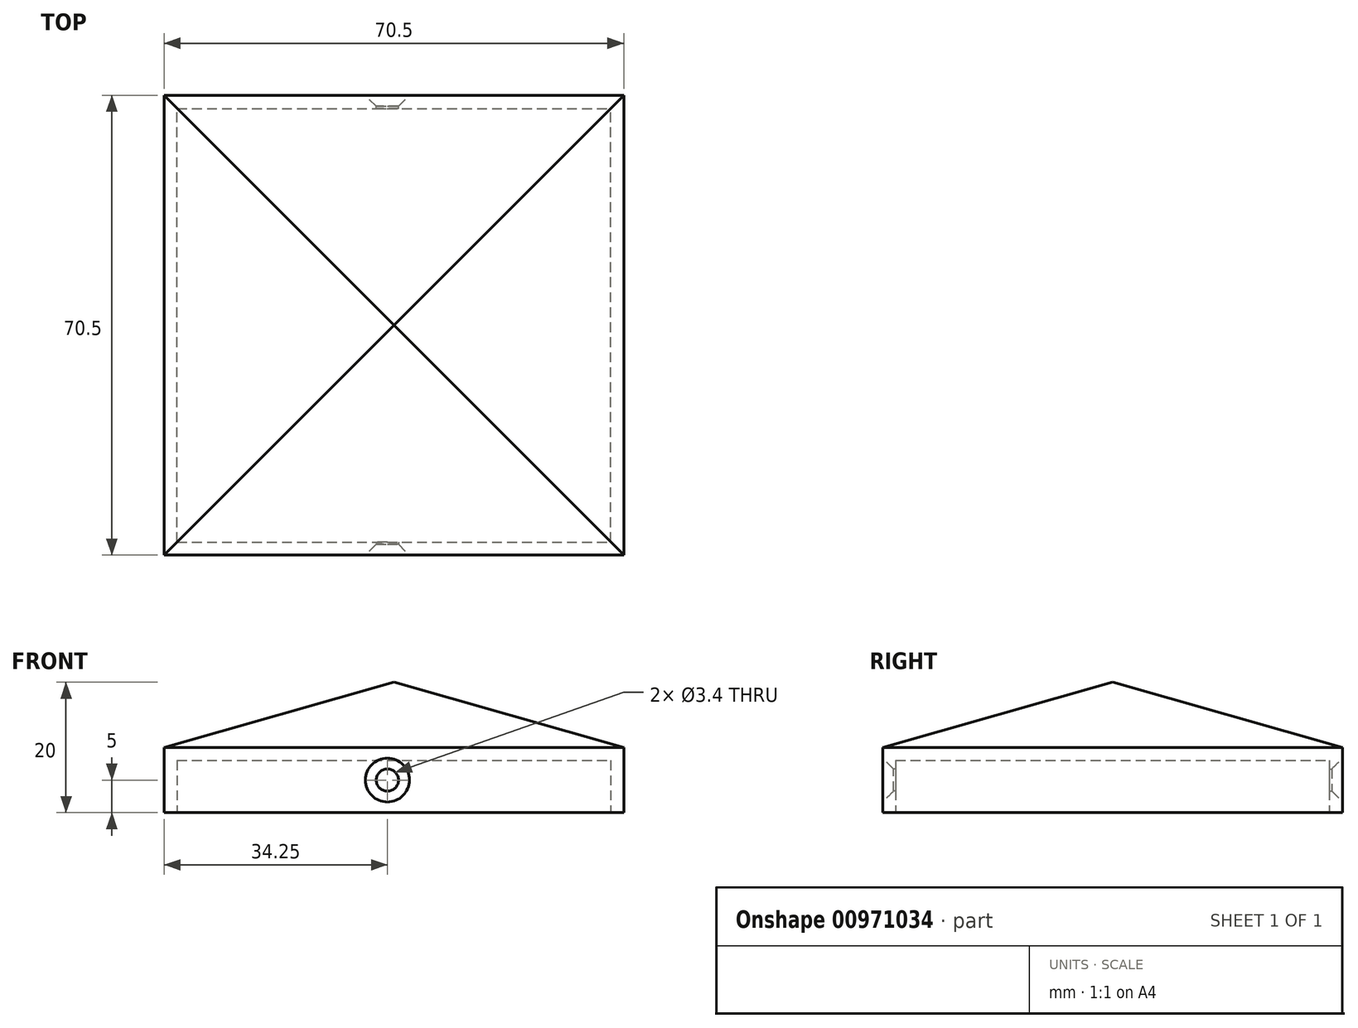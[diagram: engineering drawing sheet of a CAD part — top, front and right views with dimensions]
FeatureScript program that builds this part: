
annotation { "Feature Type Name" : "Feature", "Feature Type Description" : "" }
export const myFeature = defineFeature(function(context is Context, id is Id, definition is map)
    precondition{}
    {
        {
            var Q0;
            Q0=qCreatedBy(makeId("Top.planeOp"),FACE);
            var sketch = newSketch(context, id + "F0", { "sketchPlane" : qUnion([Q0])});
            skLineSegment(sketch, "E0.bottom", {"start": v(0, 0) * mm, "end": v(70.5, 0) * mm});
            skLineSegment(sketch, "E0.top", {"start": v(0, 70.5) * mm, "end": v(70.5, 70.5) * mm});
            skLineSegment(sketch, "E0.left", {"start": v(0, 0) * mm, "end": v(0, 70.5) * mm});
            skLineSegment(sketch, "E0.right", {"start": v(70.5, 0) * mm, "end": v(70.5, 70.5) * mm});
            skSolve(sketch);
        }
        {
            var Q0;
            Q0=makeQuery(id+"F0.imprint","IMPRINT",FACE,{"disambiguationData":[TD([[makeQuery(id+"F0.imprint","IMPRINT",EDGE,{"derivedFrom":sQuery(id+"F0.wireOp",EDGE,"E0.bottom")}),1.0]])]});
            extrude(context, id + "F1", {"entities" : qUnion([Q0]), "depth" : 10 * mm, "offsetDistance" : 25 * mm});
        }
        {
            var Q0;
            Q0=makeQuery(id+"F1.opExtrude","CAP_FACE",FACE,{"disambiguationData":[OSD([sQuery(id+"F0.wireOp",EDGE,"E0.bottom"),sQuery(id+"F0.wireOp",EDGE,"E0.top"),sQuery(id+"F0.wireOp",EDGE,"E0.left"),sQuery(id+"F0.wireOp",EDGE,"E0.right")])],"isStart":false});
            var sketch = newSketch(context, id + "F2", { "sketchPlane" : qUnion([Q0])});
            skLineSegment(sketch, "E1.bottom", {"start": v(0, 70.5) * mm, "end": v(70.5, 70.5) * mm});
            skLineSegment(sketch, "E1.top", {"start": v(0, 0) * mm, "end": v(70.5, 0) * mm});
            skLineSegment(sketch, "E1.left", {"start": v(0, 70.5) * mm, "end": v(0, 0) * mm});
            skLineSegment(sketch, "E1.right", {"start": v(70.5, 70.5) * mm, "end": v(70.5, 0) * mm});
            skSolve(sketch);
        }
        {
            var Q0;
            Q0=makeQuery(id+"F2.imprint","IMPRINT",FACE,{"disambiguationData":[TD([[makeQuery(id+"F2.imprint","IMPRINT",EDGE,{"derivedFrom":sQuery(id+"F2.wireOp",EDGE,"E1.bottom")}),-1.0]])]});
            extrude(context, id + "F3", {"entities" : qUnion([Q0]), "operationType" : NewBodyOperationType.ADD, "depth" : 10 * mm, "offsetDistance" : 25 * mm});
        }
        {
            var Q0;
            Q0=makeQuery(id+"F3.opExtrude","CAP_EDGE",EDGE,{"disambiguationData":[OSD([sQuery(id+"F2.wireOp",EDGE,"E1.bottom")])],"isStart":false});
            var Q1;
            Q1=makeQuery(id+"F3.opExtrude","CAP_EDGE",EDGE,{"disambiguationData":[OSD([sQuery(id+"F2.wireOp",EDGE,"E1.left")])],"isStart":false});
            var Q2;
            Q2=makeQuery(id+"F3.opExtrude","CAP_EDGE",EDGE,{"disambiguationData":[OSD([sQuery(id+"F2.wireOp",EDGE,"E1.top")])],"isStart":false});
            var Q3;
            Q3=makeQuery(id+"F3.opExtrude","CAP_EDGE",EDGE,{"disambiguationData":[OSD([sQuery(id+"F2.wireOp",EDGE,"E1.right")])],"isStart":false});
            chamfer(context, id + "F4", {"entities" : qUnion([Q0, Q1, Q2, Q3]), "chamferType" : ChamferType.TWO_OFFSETS, "width1" : 10 * mm, "oppositeDirection" : false, "width2" : 35.25 * mm, "tangentPropagation" : true});
        }
        {
            var Q0;
            Q0=makeQuery(id+"F1.opExtrude","CAP_FACE",FACE,{"disambiguationData":[OSD([sQuery(id+"F0.wireOp",EDGE,"E0.bottom"),sQuery(id+"F0.wireOp",EDGE,"E0.top"),sQuery(id+"F0.wireOp",EDGE,"E0.left"),sQuery(id+"F0.wireOp",EDGE,"E0.right")])],"isStart":true});
            var sketch = newSketch(context, id + "F5", { "sketchPlane" : qUnion([Q0])});
            skLineSegment(sketch, "E2.bottom", {"start": v(2, -2) * mm, "end": v(68.5, -2) * mm});
            skLineSegment(sketch, "E2.top", {"start": v(2, -68.5) * mm, "end": v(68.5, -68.5) * mm});
            skLineSegment(sketch, "E2.left", {"start": v(2, -2) * mm, "end": v(2, -68.5) * mm});
            skLineSegment(sketch, "E2.right", {"start": v(68.5, -2) * mm, "end": v(68.5, -68.5) * mm});
            skSolve(sketch);
        }
        {
            var Q0;
            Q0=makeQuery(id+"F5.imprint","IMPRINT",FACE,{"disambiguationData":[TD([[makeQuery(id+"F5.imprint","IMPRINT",EDGE,{"derivedFrom":sQuery(id+"F5.wireOp",EDGE,"E2.bottom")}),-1.0]])]});
            extrude(context, id + "F6", {"entities" : qUnion([Q0]), "operationType" : NewBodyOperationType.REMOVE, "oppositeDirection" : true, "depth" : 8 * mm, "offsetDistance" : 25 * mm});
        }
        {
            var Q0;
            Q0=makeQuery(id+"F3.boolean.opBoolean","MERGE",FACE,{"derivedFrom":[makeQuery(id+"F1.opExtrude","SWEPT_FACE",FACE,{"disambiguationData":[OSD([sQuery(id+"F0.wireOp",EDGE,"E0.bottom")])]}),makeQuery(id+"F3.opExtrude","SWEPT_FACE",FACE,{"disambiguationData":[OSD([sQuery(id+"F2.wireOp",EDGE,"E1.top")])]})]});
            var sketch = newSketch(context, id + "F7", { "sketchPlane" : qUnion([Q0])});
            skLineSegment(sketch, "E3.bottom", {"start": v(0, 0) * mm, "end": v(34.25, 0) * mm});
            skLineSegment(sketch, "E3.top", {"start": v(0, 5) * mm, "end": v(34.25, 5) * mm});
            skLineSegment(sketch, "E3.left", {"start": v(0, 0) * mm, "end": v(0, 5) * mm});
            skLineSegment(sketch, "E3.right", {"start": v(34.25, 0) * mm, "end": v(34.25, 5) * mm});
            skSolve(sketch);
        }
        {
            var Q0;
            Q0=makeQuery(id+"F3.boolean.opBoolean","MERGE",FACE,{"derivedFrom":[makeQuery(id+"F1.opExtrude","SWEPT_FACE",FACE,{"disambiguationData":[OSD([sQuery(id+"F0.wireOp",EDGE,"E0.top")])]}),makeQuery(id+"F3.opExtrude","SWEPT_FACE",FACE,{"disambiguationData":[OSD([sQuery(id+"F2.wireOp",EDGE,"E1.bottom")])]})]});
            var sketch = newSketch(context, id + "F8", { "sketchPlane" : qUnion([Q0])});
            skLineSegment(sketch, "E4.bottom", {"start": v(-34.25, 0) * mm, "end": v(0, 0) * mm});
            skLineSegment(sketch, "E4.top", {"start": v(-34.25, 5) * mm, "end": v(0, 5) * mm});
            skLineSegment(sketch, "E4.left", {"start": v(-34.25, 0) * mm, "end": v(-34.25, 5) * mm});
            skLineSegment(sketch, "E4.right", {"start": v(0, 0) * mm, "end": v(0, 5) * mm});
            skSolve(sketch);
        }
        {
            var Q0;
            Q0=sQuery(id+"F7.wireOp",VERTEX,"E3.top.end");
            var Q1;
            Q1=sQuery(id+"F8.wireOp",VERTEX,"E4.top.start");
            var Q2;
            Q2=makeQuery(id+"F1.opExtrude","SWEPT_BODY",BODY,{"disambiguationData":[OSD([sQuery(id+"F0.wireOp",EDGE,"E0.bottom"),sQuery(id+"F0.wireOp",EDGE,"E0.top"),sQuery(id+"F0.wireOp",EDGE,"E0.left"),sQuery(id+"F0.wireOp",EDGE,"E0.right")])]});
            hole(context, id + "F9", {"style" : HoleStyle.C_SINK, "endStyle" : HoleEndStyle.BLIND, "standardTappedOrClearance" : lookupTablePath({ "fit" : "Normal", "standard" : "ISO", "size" : "M3", "type" : "Clearance" }), "standardBlindInLast" : lookupTablePath({ "fit" : "Normal", "standard" : "ISO", "engagement" : "75%", "pitch" : "0.5 mm", "size" : "M3", "type" : "Clearance & tapped" }), "holeDiameter" : 3.4 * mm, "cSinkDiameter" : 6.72 * mm, "cSinkAngle" : 90 * degree, "majorDiameter" : 5 * mm, "holeDepth" : 12 * mm, "isTappedThrough" : true, "tappedDepth" : 12 * mm, "tapClearance" : 3, "locations" : qUnion([Q0, Q1]), "scope" : qUnion([Q2])});
        }
    });
